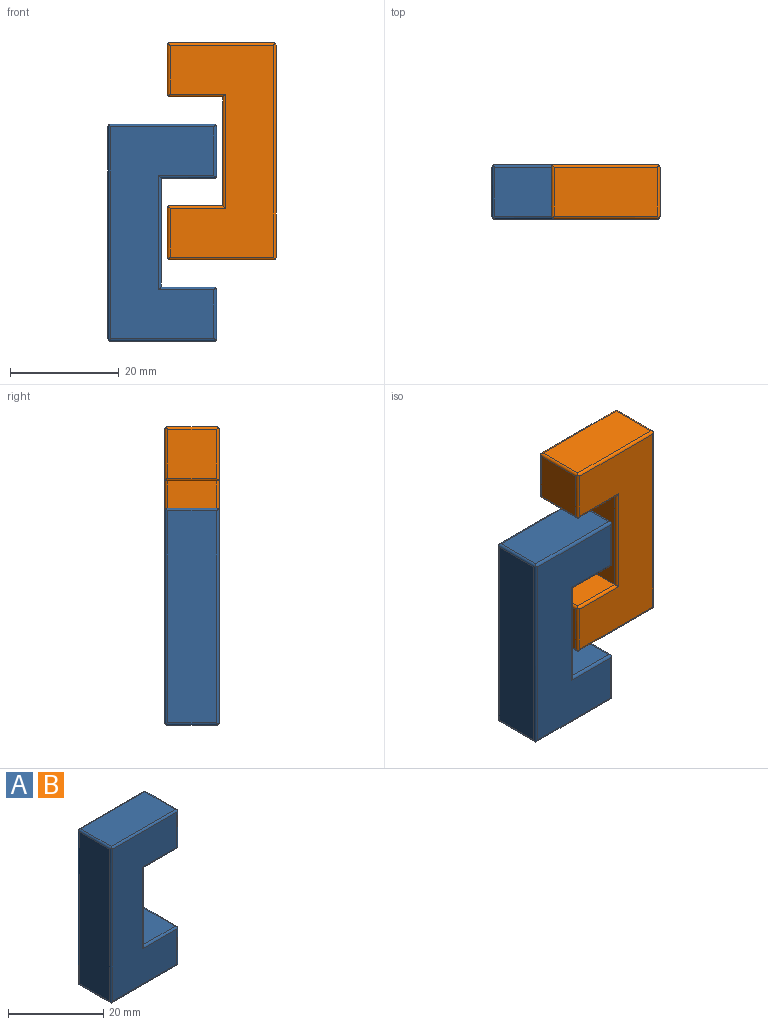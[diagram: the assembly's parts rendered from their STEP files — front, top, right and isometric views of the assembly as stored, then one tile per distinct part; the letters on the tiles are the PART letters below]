
ASSEMBLY  parts=2 mates=1
PART A: 32 faces, bbox 20x10x40 mm
  f0: plane 39x9mm, normal (-1,0,0), area 351mm2, adj f13,f21,f26,f27
  f1: plane 19x9mm, normal (0,0,-1), area 171mm2, adj f11,f19,f27,f28
  f2: plane 9x9mm, normal (1,0,0), area 81mm2, adj f10,f18,f28,f29
  f3: plane 9.66x9mm, normal (0,0,1), area 86.9mm2, adj f4,f12,f20,f29
  f4: plane 20x9mm, normal (1,0,0), area 180mm2, adj f3,f5,f14,f22
  f5: plane 9.66x9mm, normal (0,0,-1), area 86.9mm2, adj f4,f16,f24,f30
  f6: plane 9x9mm, normal (1,0,0), area 81mm2, adj f17,f25,f30,f31
  f7: plane 19x9mm, normal (0,0,1), area 171mm2, adj f15,f23,f26,f31
  f8: plane 39x19mm, normal (0,-1,0), area 527.6mm2, adj f10,f11,f12,f13,f14,f15,f16,f17
  f9: plane 39x19mm, normal (0,1,0), area 527.6mm2, adj f18,f19,f20,f21,f22,f23,f24,f25
  f10: cylinder r=0.5mm len=9.71mm, axis (0,0,-1), area 7.4mm2, adj f2,f8,f11,f12,f28,f29
  f11: cylinder r=0.5mm len=19.71mm, axis (-1,0,0), area 15.2mm2, adj f1,f8,f10,f13,f27,f28
  f12: cylinder r=0.5mm len=10.51mm, axis (1,0,0), area 7.9mm2, adj f3,f8,f10,f14,f29
  f13: cylinder r=0.5mm len=39.71mm, axis (0,0,1), area 30.9mm2, adj f0,f8,f11,f15,f26,f27
  f14: cylinder r=0.5mm len=21mm, axis (0,0,-1), area 16mm2, adj f4,f8,f12,f16
  f15: cylinder r=0.5mm len=19.71mm, axis (1,0,0), area 15.2mm2, adj f7,f8,f13,f17,f26,f31
  f16: cylinder r=0.5mm len=10.51mm, axis (-1,0,0), area 7.9mm2, adj f5,f8,f14,f17,f30
  f17: cylinder r=0.5mm len=9.71mm, axis (0,0,-1), area 7.4mm2, adj f6,f8,f15,f16,f30,f31
  f18: cylinder r=0.5mm len=9.71mm, axis (0,0,1), area 7.4mm2, adj f2,f9,f19,f20,f28,f29
  f19: cylinder r=0.5mm len=19.71mm, axis (1,0,0), area 15.2mm2, adj f1,f9,f18,f21,f27,f28
  f20: cylinder r=0.5mm len=10.51mm, axis (-1,0,0), area 7.9mm2, adj f3,f9,f18,f22,f29
  f21: cylinder r=0.5mm len=39.71mm, axis (0,0,-1), area 30.9mm2, adj f0,f9,f19,f23,f26,f27
  f22: cylinder r=0.5mm len=21mm, axis (0,0,1), area 16mm2, adj f4,f9,f20,f24
  f23: cylinder r=0.5mm len=19.71mm, axis (-1,0,0), area 15.2mm2, adj f7,f9,f21,f25,f26,f31
  f24: cylinder r=0.5mm len=10.51mm, axis (1,0,0), area 7.9mm2, adj f5,f9,f22,f25,f30
  f25: cylinder r=0.5mm len=9.71mm, axis (0,0,1), area 7.4mm2, adj f6,f9,f23,f24,f30,f31
  f26: cylinder r=0.5mm len=9.71mm, axis (0,-1,0), area 7.4mm2, adj f0,f7,f13,f15,f21,f23
  f27: cylinder r=0.5mm len=9.71mm, axis (0,1,0), area 7.4mm2, adj f0,f1,f11,f13,f19,f21
  f28: cylinder r=0.5mm len=9.71mm, axis (0,-1,0), area 7.4mm2, adj f1,f2,f10,f11,f18,f19
  f29: cylinder r=0.5mm len=9.71mm, axis (0,1,0), area 7.4mm2, adj f2,f3,f10,f12,f18,f20
  f30: cylinder r=0.5mm len=9.71mm, axis (0,-1,0), area 7.4mm2, adj f5,f6,f16,f17,f24,f25
  f31: cylinder r=0.5mm len=9.71mm, axis (0,1,0), area 7.4mm2, adj f6,f7,f15,f17,f23,f25
PART B: same geometry as A
PLACE A t=(-24.2,-15.79,20.61)mm
PLACE B rot(axis=(0,1,0),180deg) t=(-4.11,-15.79,25.01)mm
MATE slider B.f6 <-> A.f4  axis (-1,0,0) through (-18.68,-20.79,15.31)mm
